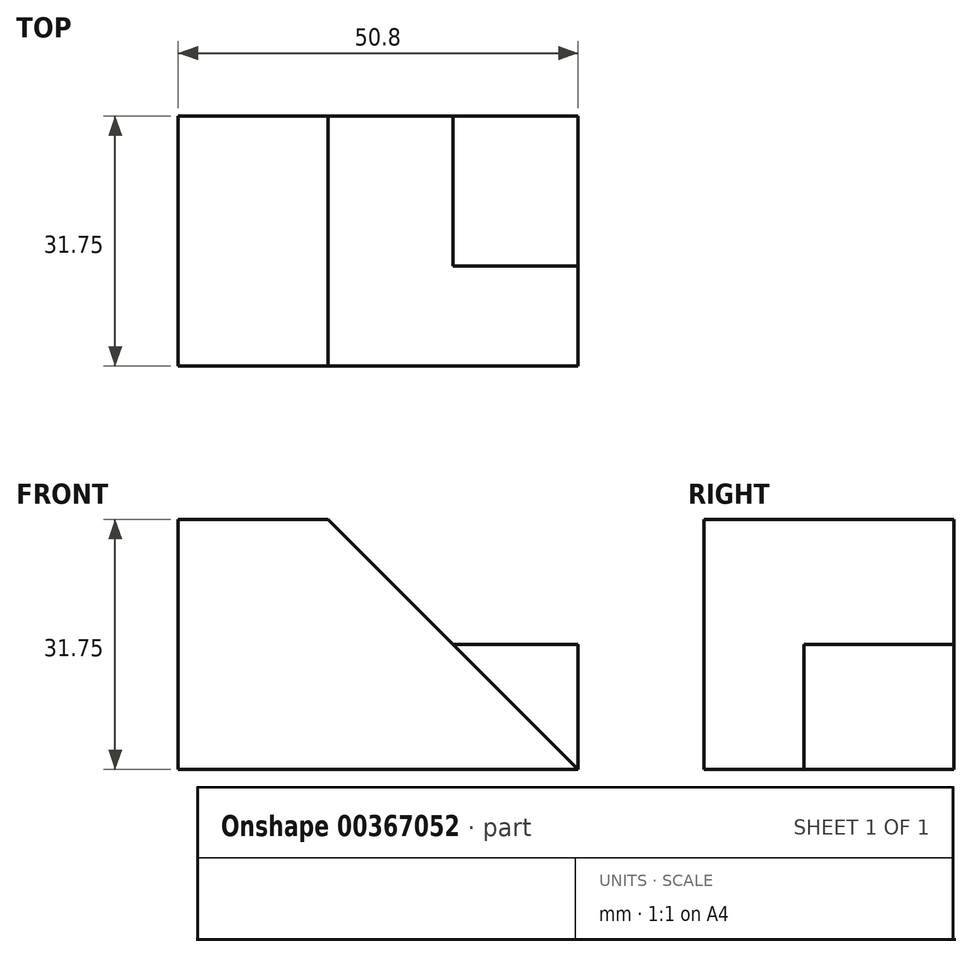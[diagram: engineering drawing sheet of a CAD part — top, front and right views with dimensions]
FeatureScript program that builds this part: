
annotation { "Feature Type Name" : "Feature", "Feature Type Description" : "" }
export const myFeature = defineFeature(function(context is Context, id is Id, definition is map)
    precondition{}
    {
        {
            var Q0;
            Q0=qCreatedBy(makeId("Front.planeOp"),FACE);
            var sketch = newSketch(context, id + "F0", { "sketchPlane" : qUnion([Q0])});
            skLineSegment(sketch, "E0", {"start": v(0, 0) * mm, "end": v(0, 31.75) * mm});
            skLineSegment(sketch, "E1", {"start": v(0, 31.75) * mm, "end": v(50.8, 31.75) * mm});
            skLineSegment(sketch, "E2", {"start": v(50.8, 31.75) * mm, "end": v(50.8, 0) * mm});
            skLineSegment(sketch, "E3", {"start": v(50.8, 0) * mm, "end": v(0, 0) * mm});
            skSolve(sketch);
        }
        {
            var Q0;
            Q0 = qSketchRegion(id + "F0", true);
            extrude(context, id + "F1", {"entities" : qUnion([Q0]), "depth" : 31.75 * mm});
        }
        {
            var Q0;
            Q0=makeQuery(id+"F1.opExtrude","CAP_FACE",FACE,{"disambiguationData":[OSD([sQuery(id+"F0.wireOp",EDGE,"E0"),sQuery(id+"F0.wireOp",EDGE,"E1"),sQuery(id+"F0.wireOp",EDGE,"E2"),sQuery(id+"F0.wireOp",EDGE,"E3")])],"isStart":false});
            var sketch = newSketch(context, id + "F2", { "sketchPlane" : qUnion([Q0])});
            skLineSegment(sketch, "E4", {"start": v(19.05, 31.75) * mm, "end": v(50.8, 0) * mm});
            skSolve(sketch);
        }
        {
            var Q0;
            {var subQ0=sQuery(id+"F2.wireOp",EDGE,"E4");Q0=makeQuery(id+"F2.imprint","IMPRINT",FACE,{"disambiguationData":[TD([[makeQuery(id+"F2.imprint","IMPRINT",EDGE,{"derivedFrom":subQ0}),1.0]])]});}
            extrude(context, id + "F3", {"entities" : qUnion([Q0]), "operationType" : NewBodyOperationType.REMOVE, "oppositeDirection" : true, "depth" : 12.7 * mm});
        }
        {
            var Q0;
            Q0=makeQuery(id+"F3.boolean.opBoolean","COPY",FACE,{"derivedFrom":makeQuery(id+"F3.opExtrude","CAP_FACE",FACE,{"disambiguationData":[OSD([sQuery(id+"F0.wireOp",EDGE,"E1"),sQuery(id+"F0.wireOp",EDGE,"E2"),sQuery(id+"F2.wireOp",EDGE,"E4")])],"isStart":false})});
            var sketch = newSketch(context, id + "F4", { "sketchPlane" : qUnion([Q0])});
            skLineSegment(sketch, "E5", {"start": v(34.93, 15.87) * mm, "end": v(50.8, 15.87) * mm});
            skSolve(sketch);
        }
        {
            var Q0;
            Q0 = qSketchRegion(id + "F4", true);
            var Q1;
            {var subQ0=sQuery(id+"F4.wireOp",EDGE,"E5");Q1=makeQuery(id+"F4.imprint","IMPRINT",FACE,{"disambiguationData":[TD([[makeQuery(id+"F4.imprint","IMPRINT",EDGE,{"derivedFrom":subQ0}),1.0]])]});}
            extrude(context, id + "F5", {"entities" : qUnion([Q0, Q1]), "operationType" : NewBodyOperationType.REMOVE, "oppositeDirection" : true, "depth" : 25.4 * mm});
        }
    });
